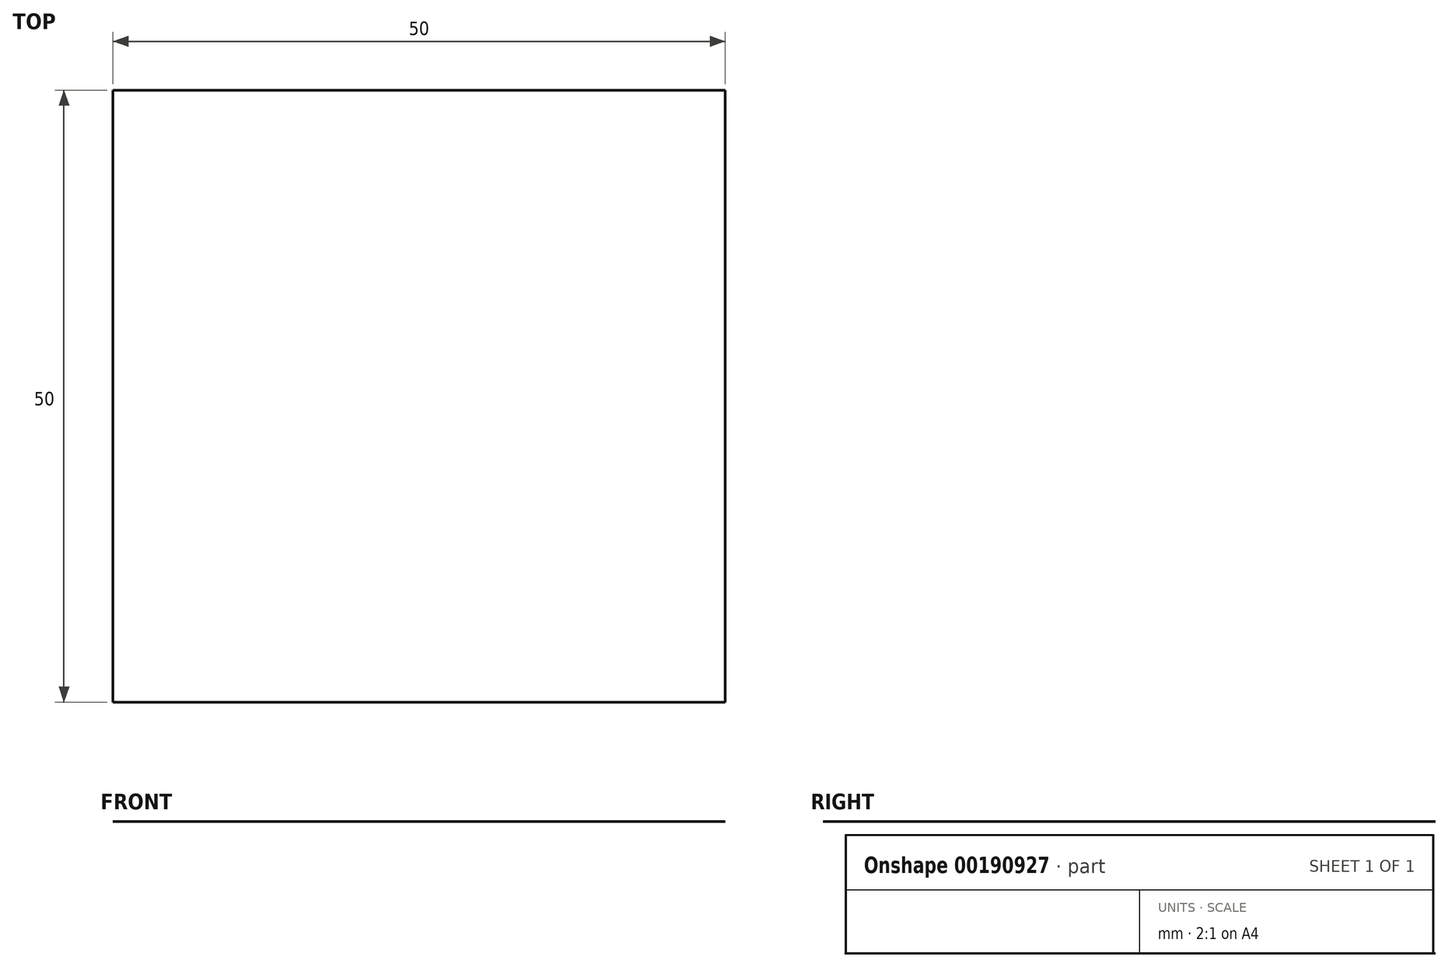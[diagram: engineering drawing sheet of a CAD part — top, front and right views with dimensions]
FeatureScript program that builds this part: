
annotation { "Feature Type Name" : "Feature", "Feature Type Description" : "" }
export const myFeature = defineFeature(function(context is Context, id is Id, definition is map)
    precondition{}
    {
        {
            var Q0;
            Q0=qCreatedBy(makeId("Top.planeOp"),FACE);
            var sketch = newSketch(context, id + "F0", { "sketchPlane" : qUnion([Q0])});
            skLineSegment(sketch, "E0.bottom", {"start": v(25, 25) * mm, "end": v(-25, 25) * mm});
            skLineSegment(sketch, "E0.top", {"start": v(25, -25) * mm, "end": v(-25, -25) * mm});
            skLineSegment(sketch, "E0.left", {"start": v(25, 25) * mm, "end": v(25, -25) * mm});
            skLineSegment(sketch, "E0.right", {"start": v(-25, 25) * mm, "end": v(-25, -25) * mm});
            skPoint(sketch, "E0.middle", {"position": v(0, 0) * mm});
            skSolve(sketch);
        }
        {
            var Q0;
            Q0=sQuery(id+"F0.wireOp",EDGE,"E0.bottom");
            var Q1;
            Q1=sQuery(id+"F0.wireOp",EDGE,"E0.top");
            loft(context, id + "F1", {"bodyType" : ToolBodyType.SURFACE, "wireProfilesArray" : [{ "wireProfileEntities" : qUnion([Q0]) }, { "wireProfileEntities" : qUnion([Q1]) }]});
        }
        {
            var Q0;
            Q0=qCreatedBy(makeId("Top.planeOp"),FACE);
            cPlane(context, id + "F2", {"entities" : qUnion([Q0]), "cplaneType" : CPlaneType.OFFSET, "offset" : 156 * mm, "width" : 150 * mm, "height" : 150 * mm});
        }
    });
